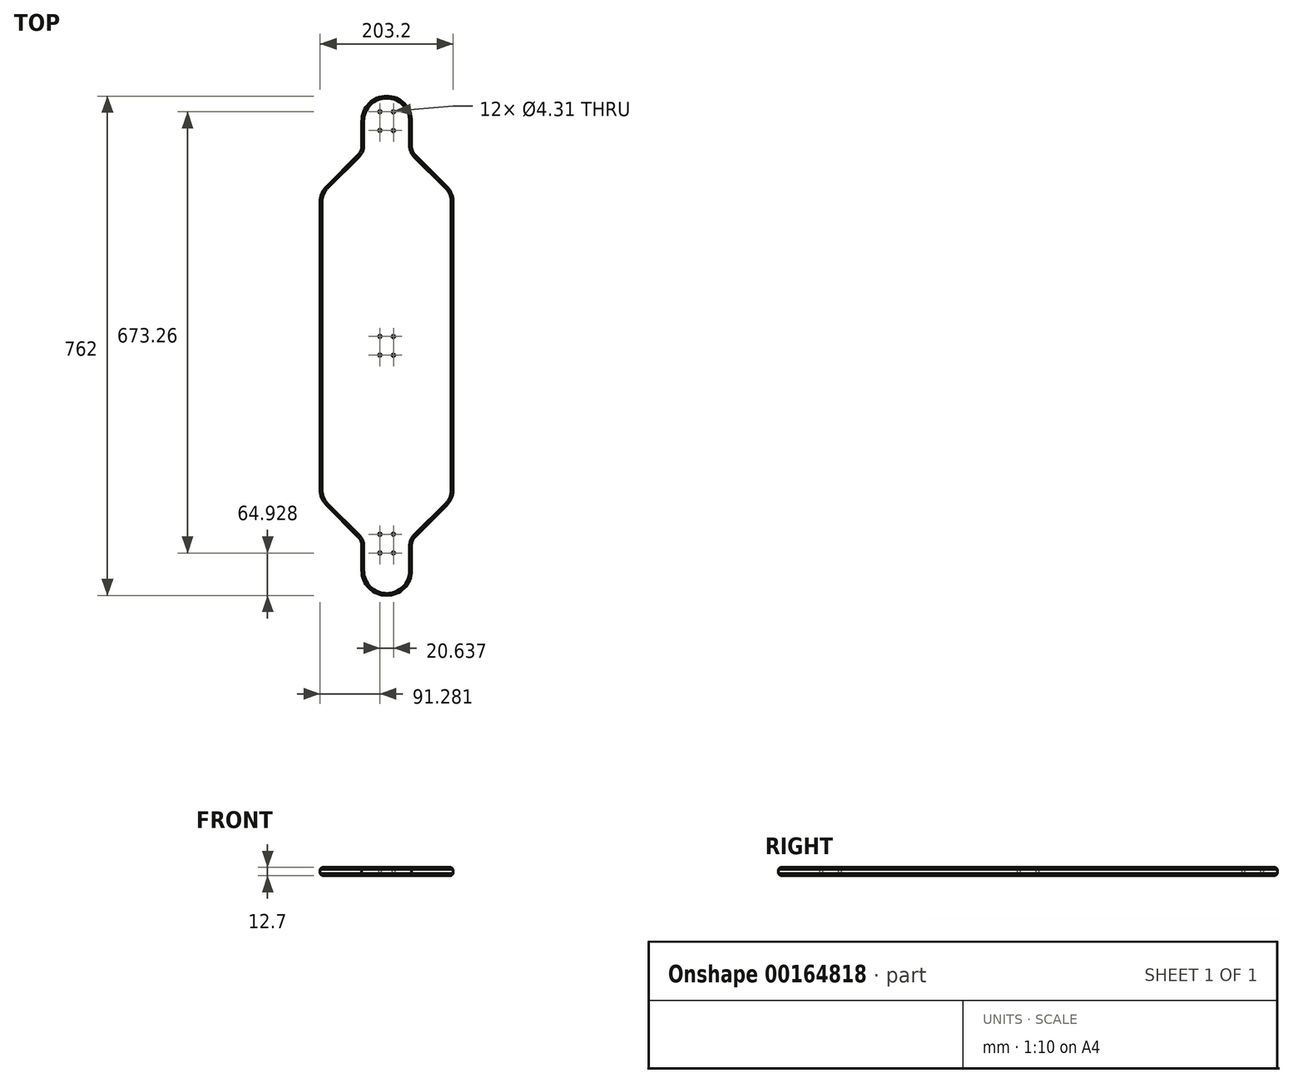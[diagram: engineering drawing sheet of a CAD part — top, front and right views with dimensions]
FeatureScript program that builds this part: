
annotation { "Feature Type Name" : "Feature", "Feature Type Description" : "" }
export const myFeature = defineFeature(function(context is Context, id is Id, definition is map)
    precondition{}
    {
        {
            var Q0;
            Q0=qCreatedBy(makeId("Top.planeOp"),FACE);
            var sketch = newSketch(context, id + "F0", { "sketchPlane" : qUnion([Q0])});
            skArc(sketch, "E0", {"start": v(-38.1, 0) * mm, "mid": v(0, -38.1) * mm, "end": v(38.1, 0) * mm});
            skLineSegment(sketch, "E1.bottom", {"start": v(-38.1, 0) * mm, "end": v(38.1, 0) * mm, "construction": true});
            skLineSegment(sketch, "E1.top", {"start": v(-38.1, 38.1) * mm, "end": v(38.1, 38.1) * mm, "construction": true});
            skLineSegment(sketch, "E1.left", {"start": v(-38.1, 0) * mm, "end": v(-38.1, 38.1) * mm});
            skLineSegment(sketch, "E1.right", {"start": v(38.1, 0) * mm, "end": v(38.1, 38.1) * mm});
            skArc(sketch, "E2", {"start": v(-38.1, 38.1) * mm, "mid": v(-39.55, 45.4) * mm, "end": v(-43.68, 51.57) * mm});
            skLineSegment(sketch, "E3", {"start": v(-43.68, 51.57) * mm, "end": v(-92.3, 100.2) * mm});
            skArc(sketch, "E4", {"start": v(-101.6, 122.64) * mm, "mid": v(-99.18, 110.5) * mm, "end": v(-92.3, 100.2) * mm});
            skLineSegment(sketch, "E5.bottom", {"start": v(-101.6, 122.64) * mm, "end": v(101.6, 122.64) * mm, "construction": true});
            skLineSegment(sketch, "E5.top", {"start": v(-101.6, 563.16) * mm, "end": v(101.6, 563.16) * mm, "construction": true});
            skLineSegment(sketch, "E5.left", {"start": v(-101.6, 122.64) * mm, "end": v(-101.6, 563.16) * mm});
            skLineSegment(sketch, "E5.right", {"start": v(101.6, 122.64) * mm, "end": v(101.6, 563.16) * mm});
            skLineSegment(sketch, "E6", {"start": v(0, 38.1) * mm, "end": v(0, 122.64) * mm, "construction": true});
            skArc(sketch, "E7", {"start": v(43.68, 51.57) * mm, "mid": v(39.55, 45.4) * mm, "end": v(38.1, 38.1) * mm});
            skArc(sketch, "E8", {"start": v(92.3, 100.2) * mm, "mid": v(99.18, 110.5) * mm, "end": v(101.6, 122.64) * mm});
            skLineSegment(sketch, "E9", {"start": v(92.3, 100.2) * mm, "end": v(43.68, 51.57) * mm});
            skLineSegment(sketch, "E10", {"start": v(-43.68, 51.57) * mm, "end": v(-43.68, 100.2) * mm, "construction": true});
            skLineSegment(sketch, "E11", {"start": v(-43.68, 100.2) * mm, "end": v(-92.3, 100.2) * mm, "construction": true});
            skArc(sketch, "E12", {"start": v(101.6, 563.16) * mm, "mid": v(99.18, 575.3) * mm, "end": v(92.3, 585.6) * mm});
            skArc(sketch, "E13", {"start": v(-92.3, 585.6) * mm, "mid": v(-99.18, 575.3) * mm, "end": v(-101.6, 563.16) * mm});
            skLineSegment(sketch, "E14", {"start": v(0, 563.16) * mm, "end": v(0, 647.7) * mm, "construction": true});
            skLineSegment(sketch, "E15.bottom", {"start": v(38.1, 647.7) * mm, "end": v(-38.1, 647.7) * mm, "construction": true});
            skLineSegment(sketch, "E15.top", {"start": v(38.1, 685.8) * mm, "end": v(-38.1, 685.8) * mm, "construction": true});
            skLineSegment(sketch, "E15.left", {"start": v(38.1, 647.7) * mm, "end": v(38.1, 685.8) * mm});
            skLineSegment(sketch, "E15.right", {"start": v(-38.1, 647.7) * mm, "end": v(-38.1, 685.8) * mm});
            skArc(sketch, "E16", {"start": v(38.1, 685.8) * mm, "mid": v(0, 723.9) * mm, "end": v(-38.1, 685.8) * mm});
            skArc(sketch, "E17", {"start": v(-43.68, 634.23) * mm, "mid": v(-39.55, 640.4) * mm, "end": v(-38.1, 647.7) * mm});
            skArc(sketch, "E18", {"start": v(38.1, 647.7) * mm, "mid": v(39.55, 640.4) * mm, "end": v(43.68, 634.23) * mm});
            skLineSegment(sketch, "E19", {"start": v(-43.68, 634.23) * mm, "end": v(-92.3, 585.6) * mm});
            skLineSegment(sketch, "E20", {"start": v(43.68, 634.23) * mm, "end": v(92.3, 585.6) * mm});
            skSolve(sketch);
        }
        {
            var Q0;
            Q0 = qSketchRegion(id + "F0", true);
            extrude(context, id + "F1", {"entities" : qUnion([Q0]), "depth" : 12.7 * mm});
        }
        {
            var Q0;
            Q0=makeQuery(id+"F1.opExtrude","CAP_FACE",FACE,{"disambiguationData":[OSD([sQuery(id+"F0.wireOp",EDGE,"E0"),sQuery(id+"F0.wireOp",EDGE,"E1.left"),sQuery(id+"F0.wireOp",EDGE,"E1.right"),sQuery(id+"F0.wireOp",EDGE,"E2"),sQuery(id+"F0.wireOp",EDGE,"E3"),sQuery(id+"F0.wireOp",EDGE,"E4"),sQuery(id+"F0.wireOp",EDGE,"E5.left"),sQuery(id+"F0.wireOp",EDGE,"E5.right"),sQuery(id+"F0.wireOp",EDGE,"E7"),sQuery(id+"F0.wireOp",EDGE,"E8"),sQuery(id+"F0.wireOp",EDGE,"E9"),sQuery(id+"F0.wireOp",EDGE,"E12"),sQuery(id+"F0.wireOp",EDGE,"E13"),sQuery(id+"F0.wireOp",EDGE,"E15.left"),sQuery(id+"F0.wireOp",EDGE,"E15.right"),sQuery(id+"F0.wireOp",EDGE,"E16"),sQuery(id+"F0.wireOp",EDGE,"E17"),sQuery(id+"F0.wireOp",EDGE,"E18"),sQuery(id+"F0.wireOp",EDGE,"E19"),sQuery(id+"F0.wireOp",EDGE,"E20")])],"isStart":true});
            var Q1;
            Q1=makeQuery(id+"F1.opExtrude","CAP_FACE",FACE,{"disambiguationData":[OSD([sQuery(id+"F0.wireOp",EDGE,"E0"),sQuery(id+"F0.wireOp",EDGE,"E1.left"),sQuery(id+"F0.wireOp",EDGE,"E1.right"),sQuery(id+"F0.wireOp",EDGE,"E2"),sQuery(id+"F0.wireOp",EDGE,"E3"),sQuery(id+"F0.wireOp",EDGE,"E4"),sQuery(id+"F0.wireOp",EDGE,"E5.left"),sQuery(id+"F0.wireOp",EDGE,"E5.right"),sQuery(id+"F0.wireOp",EDGE,"E7"),sQuery(id+"F0.wireOp",EDGE,"E8"),sQuery(id+"F0.wireOp",EDGE,"E9"),sQuery(id+"F0.wireOp",EDGE,"E12"),sQuery(id+"F0.wireOp",EDGE,"E13"),sQuery(id+"F0.wireOp",EDGE,"E15.left"),sQuery(id+"F0.wireOp",EDGE,"E15.right"),sQuery(id+"F0.wireOp",EDGE,"E16"),sQuery(id+"F0.wireOp",EDGE,"E17"),sQuery(id+"F0.wireOp",EDGE,"E18"),sQuery(id+"F0.wireOp",EDGE,"E19"),sQuery(id+"F0.wireOp",EDGE,"E20")])],"isStart":false});
            chamfer(context, id + "F2", {"entities" : qUnion([Q0, Q1]), "width" : 3.17 * mm, "tangentPropagation" : true});
        }
        {
            var Q0;
            Q0=makeQuery(id+"F1.opExtrude","CAP_FACE",FACE,{"disambiguationData":[OSD([sQuery(id+"F0.wireOp",EDGE,"E0"),sQuery(id+"F0.wireOp",EDGE,"E1.left"),sQuery(id+"F0.wireOp",EDGE,"E1.right"),sQuery(id+"F0.wireOp",EDGE,"E2"),sQuery(id+"F0.wireOp",EDGE,"E3"),sQuery(id+"F0.wireOp",EDGE,"E4"),sQuery(id+"F0.wireOp",EDGE,"E5.left"),sQuery(id+"F0.wireOp",EDGE,"E5.right"),sQuery(id+"F0.wireOp",EDGE,"E7"),sQuery(id+"F0.wireOp",EDGE,"E8"),sQuery(id+"F0.wireOp",EDGE,"E9"),sQuery(id+"F0.wireOp",EDGE,"E12"),sQuery(id+"F0.wireOp",EDGE,"E13"),sQuery(id+"F0.wireOp",EDGE,"E15.left"),sQuery(id+"F0.wireOp",EDGE,"E15.right"),sQuery(id+"F0.wireOp",EDGE,"E16"),sQuery(id+"F0.wireOp",EDGE,"E17"),sQuery(id+"F0.wireOp",EDGE,"E18"),sQuery(id+"F0.wireOp",EDGE,"E19"),sQuery(id+"F0.wireOp",EDGE,"E20")])],"isStart":true});
            var sketch = newSketch(context, id + "F3", { "sketchPlane" : qUnion([Q0])});
            skLineSegment(sketch, "E21", {"start": v(-98.42, -342.9) * mm, "end": v(98.42, -342.9) * mm, "construction": true});
            skLineSegment(sketch, "E22", {"start": v(0, -342.9) * mm, "end": v(0, -41.12) * mm, "construction": true});
            skLineSegment(sketch, "E23", {"start": v(0, -342.9) * mm, "end": v(0, -685.8) * mm, "construction": true});
            skLineSegment(sketch, "E24.bottom", {"start": v(-10.32, -357.19) * mm, "end": v(10.32, -357.19) * mm, "construction": true});
            skLineSegment(sketch, "E24.top", {"start": v(-10.32, -328.61) * mm, "end": v(10.32, -328.61) * mm, "construction": true});
            skLineSegment(sketch, "E24.left", {"start": v(-10.32, -357.19) * mm, "end": v(-10.32, -328.61) * mm, "construction": true});
            skLineSegment(sketch, "E24.right", {"start": v(10.32, -357.19) * mm, "end": v(10.32, -328.61) * mm, "construction": true});
            skPoint(sketch, "E24.middle", {"position": v(0, -342.9) * mm});
            skLineSegment(sketch, "E25.bottom", {"start": v(-10.32, -671.51) * mm, "end": v(10.32, -671.51) * mm, "construction": true});
            skLineSegment(sketch, "E25.top", {"start": v(-10.32, -700.09) * mm, "end": v(10.32, -700.09) * mm, "construction": true});
            skLineSegment(sketch, "E25.left", {"start": v(-10.32, -671.51) * mm, "end": v(-10.32, -700.09) * mm, "construction": true});
            skLineSegment(sketch, "E25.right", {"start": v(10.32, -671.51) * mm, "end": v(10.32, -700.09) * mm, "construction": true});
            skPoint(sketch, "E25.middle", {"position": v(0, -685.8) * mm});
            skLineSegment(sketch, "E26.bottom", {"start": v(-10.32, -26.83) * mm, "end": v(10.32, -26.83) * mm, "construction": true});
            skLineSegment(sketch, "E26.top", {"start": v(-10.32, -55.4) * mm, "end": v(10.32, -55.4) * mm, "construction": true});
            skLineSegment(sketch, "E26.left", {"start": v(-10.32, -26.83) * mm, "end": v(-10.32, -55.4) * mm, "construction": true});
            skLineSegment(sketch, "E26.right", {"start": v(10.32, -26.83) * mm, "end": v(10.32, -55.4) * mm, "construction": true});
            skPoint(sketch, "E26.middle", {"position": v(0, -41.12) * mm});
            skCircle(sketch, "E27", {"center": v(10.32, -700.09) * mm, "radius": 2.15 * mm});
            skCircle(sketch, "E28", {"center": v(10.32, -671.51) * mm, "radius": 2.15 * mm});
            skCircle(sketch, "E29", {"center": v(-10.32, -671.51) * mm, "radius": 2.15 * mm});
            skCircle(sketch, "E30", {"center": v(-10.32, -700.09) * mm, "radius": 2.15 * mm});
            skCircle(sketch, "E31", {"center": v(10.32, -55.4) * mm, "radius": 2.15 * mm});
            skCircle(sketch, "E32", {"center": v(10.32, -26.83) * mm, "radius": 2.15 * mm});
            skCircle(sketch, "E33", {"center": v(-10.32, -55.4) * mm, "radius": 2.15 * mm});
            skCircle(sketch, "E34", {"center": v(-10.32, -26.83) * mm, "radius": 2.15 * mm});
            skCircle(sketch, "E35", {"center": v(10.32, -357.19) * mm, "radius": 2.15 * mm});
            skCircle(sketch, "E36", {"center": v(10.32, -328.61) * mm, "radius": 2.15 * mm});
            skCircle(sketch, "E37", {"center": v(-10.32, -328.61) * mm, "radius": 2.15 * mm});
            skCircle(sketch, "E38", {"center": v(-10.32, -357.19) * mm, "radius": 2.15 * mm});
            skLineSegment(sketch, "E39", {"start": v(0, -41.12) * mm, "end": v(34.92, -41.12) * mm, "construction": true});
            skLineSegment(sketch, "E40", {"start": v(-41.43, -53.82) * mm, "end": v(-20.72, -53.82) * mm, "construction": true});
            skLineSegment(sketch, "E41", {"start": v(-20.72, -53.82) * mm, "end": v(-20.72, -41.12) * mm, "construction": true});
            skLineSegment(sketch, "E42", {"start": v(-20.72, -41.12) * mm, "end": v(0, -41.12) * mm, "construction": true});
            skSolve(sketch);
        }
        {
            var Q0;
            Q0 = qSketchRegion(id + "F3", true);
            var Q1;
            Q1=makeQuery(id+"F1.opExtrude","CAP_FACE",FACE,{"disambiguationData":[OSD([sQuery(id+"F0.wireOp",EDGE,"E0"),sQuery(id+"F0.wireOp",EDGE,"E1.left"),sQuery(id+"F0.wireOp",EDGE,"E1.right"),sQuery(id+"F0.wireOp",EDGE,"E2"),sQuery(id+"F0.wireOp",EDGE,"E3"),sQuery(id+"F0.wireOp",EDGE,"E4"),sQuery(id+"F0.wireOp",EDGE,"E5.left"),sQuery(id+"F0.wireOp",EDGE,"E5.right"),sQuery(id+"F0.wireOp",EDGE,"E7"),sQuery(id+"F0.wireOp",EDGE,"E8"),sQuery(id+"F0.wireOp",EDGE,"E9"),sQuery(id+"F0.wireOp",EDGE,"E12"),sQuery(id+"F0.wireOp",EDGE,"E13"),sQuery(id+"F0.wireOp",EDGE,"E15.left"),sQuery(id+"F0.wireOp",EDGE,"E15.right"),sQuery(id+"F0.wireOp",EDGE,"E16"),sQuery(id+"F0.wireOp",EDGE,"E17"),sQuery(id+"F0.wireOp",EDGE,"E18"),sQuery(id+"F0.wireOp",EDGE,"E19"),sQuery(id+"F0.wireOp",EDGE,"E20")])],"isStart":false});
            extrude(context, id + "F4", {"entities" : qUnion([Q0]), "operationType" : NewBodyOperationType.REMOVE, "endBound" : BoundingType.UP_TO_SURFACE, "oppositeDirection" : true, "endBoundEntityFace" : qUnion([Q1]), "depth" : 25.4 * mm});
        }
    });
